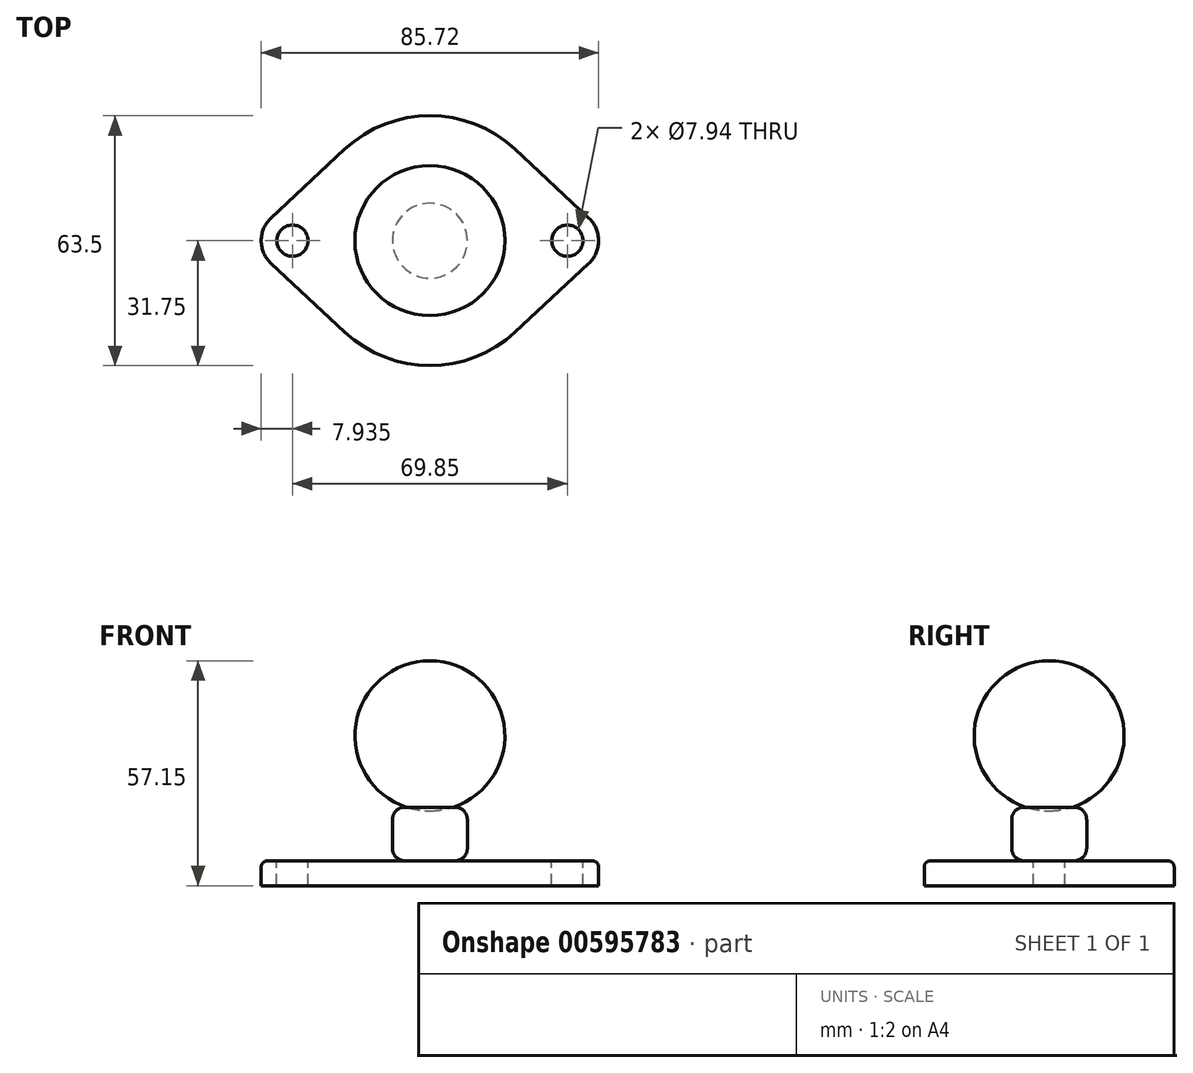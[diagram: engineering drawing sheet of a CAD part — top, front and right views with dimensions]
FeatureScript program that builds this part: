
annotation { "Feature Type Name" : "Feature", "Feature Type Description" : "" }
export const myFeature = defineFeature(function(context is Context, id is Id, definition is map)
    precondition{}
    {
        {
            var Q0;
            Q0=qCreatedBy(makeId("Top.planeOp"),FACE);
            var sketch = newSketch(context, id + "F0", { "sketchPlane" : qUnion([Q0])});
            skArc(sketch, "E0", {"start": v(21.65, 23.23) * mm, "mid": v(0, 31.75) * mm, "end": v(-21.65, 23.23) * mm});
            skLineSegment(sketch, "E1", {"start": v(0, 0) * mm, "end": v(34.93, 0) * mm});
            skCircle(sketch, "E2", {"center": v(34.93, 0) * mm, "radius": 3.97 * mm});
            skArc(sketch, "E3", {"start": v(40.34, -5.8) * mm, "mid": v(42.86, 0) * mm, "end": v(40.34, 5.8) * mm});
            skLineSegment(sketch, "E4", {"start": v(21.65, 23.23) * mm, "end": v(40.34, 5.8) * mm});
            skLineSegment(sketch, "E5.MirrorCS", {"start": v(21.65, -23.23) * mm, "end": v(40.34, -5.8) * mm});
            skLineSegment(sketch, "E6", {"start": v(0, 0) * mm, "end": v(0, 37.31) * mm});
            skLineSegment(sketch, "E7.MirrorCS", {"start": v(-21.65, 23.23) * mm, "end": v(-40.34, 5.8) * mm});
            skArc(sketch, "E8.MirrorC", {"start": v(-40.34, -5.8) * mm, "mid": v(-42.86, 0) * mm, "end": v(-40.34, 5.8) * mm});
            skLineSegment(sketch, "E9.MirrorCS", {"start": v(-21.65, -23.23) * mm, "end": v(-40.34, -5.8) * mm});
            skCircle(sketch, "E10.MirrorC", {"center": v(-34.93, 0) * mm, "radius": 3.97 * mm});
            skArc(sketch, "E11.trimOffspring", {"start": v(-21.65, -23.23) * mm, "mid": v(0, -31.75) * mm, "end": v(21.65, -23.23) * mm});
            skCircle(sketch, "E12", {"center": v(0, 0) * mm, "radius": 9.53 * mm});
            skSolve(sketch);
        }
        {
            var Q0;
            Q0=makeQuery(id+"F0.imprint","IMPRINT",FACE,{"disambiguationData":[TD([[makeQuery(id+"F0.imprint","IMPRINT",EDGE,{"derivedFrom":sQuery(id+"F0.wireOp",EDGE,"E2")}),-1.0]])]});
            var Q1;
            {var subQ0=sQuery(id+"F0.wireOp",EDGE,"E6");var subQ1=sQuery(id+"F0.wireOp",EDGE,"E1");var subQ2=makeQuery(id+"F0.imprint","INTERSECT",VERTEX,{"derivedFrom":[subQ1,subQ0]});Q1=makeQuery(id+"F0.imprint","IMPRINT",FACE,{"disambiguationData":[TD([[makeQuery(id+"F0.imprint","IMPRINT",EDGE,{"disambiguationData":[TD([[subQ2,-1.0]])],"derivedFrom":subQ1}),-1.0]])]});}
            var Q2;
            {var subQ0=sQuery(id+"F0.wireOp",EDGE,"E6");var subQ1=sQuery(id+"F0.wireOp",EDGE,"E1");var subQ2=makeQuery(id+"F0.imprint","INTERSECT",VERTEX,{"derivedFrom":[subQ1,subQ0]});Q2=makeQuery(id+"F0.imprint","IMPRINT",FACE,{"disambiguationData":[TD([[makeQuery(id+"F0.imprint","IMPRINT",EDGE,{"disambiguationData":[TD([[subQ2,-1.0]])],"derivedFrom":subQ1}),1.0]])]});}
            extrude(context, id + "F1", {"entities" : qUnion([Q0, Q1, Q2]), "oppositeDirection" : true, "depth" : 6.35 * mm, "offsetDistance" : 25.4 * mm});
        }
        {
            var Q0;
            Q0=qCreatedBy(makeId("Front.planeOp"),FACE);
            var sketch = newSketch(context, id + "F2", { "sketchPlane" : qUnion([Q0])});
            skLineSegment(sketch, "E13", {"start": v(0, 0) * mm, "end": v(0, 50.8) * mm});
            skCircle(sketch, "E14", {"center": v(0, 31.75) * mm, "radius": 19.05 * mm});
            skSolve(sketch);
        }
        {
            var Q0;
            {var subQ0=sQuery(id+"F2.wireOp",EDGE,"E14");var subQ1=sQuery(id+"F2.wireOp",EDGE,"E13");var subQ2=makeQuery(id+"F2.imprint","INTERSECT",VERTEX,{"disambiguationData":[OD(0.0)],"derivedFrom":[subQ1,subQ0]});Q0=makeQuery(id+"F2.imprint","IMPRINT",FACE,{"disambiguationData":[TD([[makeQuery(id+"F2.imprint","IMPRINT",EDGE,{"disambiguationData":[TD([[subQ2,1.0]])],"derivedFrom":subQ1}),-1.0]])]});}
            var Q1;
            Q1=sQuery(id+"F2.wireOp",EDGE,"E13");
            revolve(context, id + "F3", {"entities" : qUnion([Q0]), "axis" : qUnion([Q1]), "revolveType" : RevolveType.FULL});
        }
        {
            var Q0;
            {var subQ0=sQuery(id+"F0.wireOp",EDGE,"E6");var subQ1=sQuery(id+"F0.wireOp",EDGE,"E1");var subQ2=makeQuery(id+"F0.imprint","INTERSECT",VERTEX,{"derivedFrom":[subQ1,subQ0]});Q0=makeQuery(id+"F0.imprint","IMPRINT",FACE,{"disambiguationData":[TD([[makeQuery(id+"F0.imprint","IMPRINT",EDGE,{"disambiguationData":[TD([[subQ2,-1.0]])],"derivedFrom":subQ1}),-1.0]])]});}
            var Q1;
            {var subQ0=sQuery(id+"F0.wireOp",EDGE,"E6");var subQ1=sQuery(id+"F0.wireOp",EDGE,"E1");var subQ2=makeQuery(id+"F0.imprint","INTERSECT",VERTEX,{"derivedFrom":[subQ1,subQ0]});Q1=makeQuery(id+"F0.imprint","IMPRINT",FACE,{"disambiguationData":[TD([[makeQuery(id+"F0.imprint","IMPRINT",EDGE,{"disambiguationData":[TD([[subQ2,-1.0]])],"derivedFrom":subQ1}),1.0]])]});}
            extrude(context, id + "F4", {"entities" : qUnion([Q0, Q1]), "endBound" : BoundingType.UP_TO_NEXT, "depth" : 25.4 * mm, "offsetDistance" : 25.4 * mm});
        }
        {
            var Q0;
            Q0=makeQuery(id+"F1.opExtrude","CAP_EDGE",EDGE,{"disambiguationData":[OSD([sQuery(id+"F0.wireOp",EDGE,"E11.trimOffspring")])],"isStart":true});
            fillet(context, id + "F5", {"entities" : qUnion([Q0]), "radius" : 1.6 * mm, "tangentPropagation" : true, "allowEdgeOverflow" : false});
        }
        {
            var Q0;
            Q0=makeQuery(id+"F4.opExtrude","CAP_EDGE",EDGE,{"disambiguationData":[OSD([sQuery(id+"F0.wireOp",EDGE,"E12")])],"isStart":false});
            var Q1;
            Q1=makeQuery(id+"F4.opExtrude","CAP_EDGE",EDGE,{"disambiguationData":[OSD([sQuery(id+"F0.wireOp",EDGE,"E12")])],"isStart":true});
            fillet(context, id + "F6", {"entities" : qUnion([Q0, Q1]), "radius" : 3.17 * mm, "tangentPropagation" : true, "allowEdgeOverflow" : false});
        }
    });
